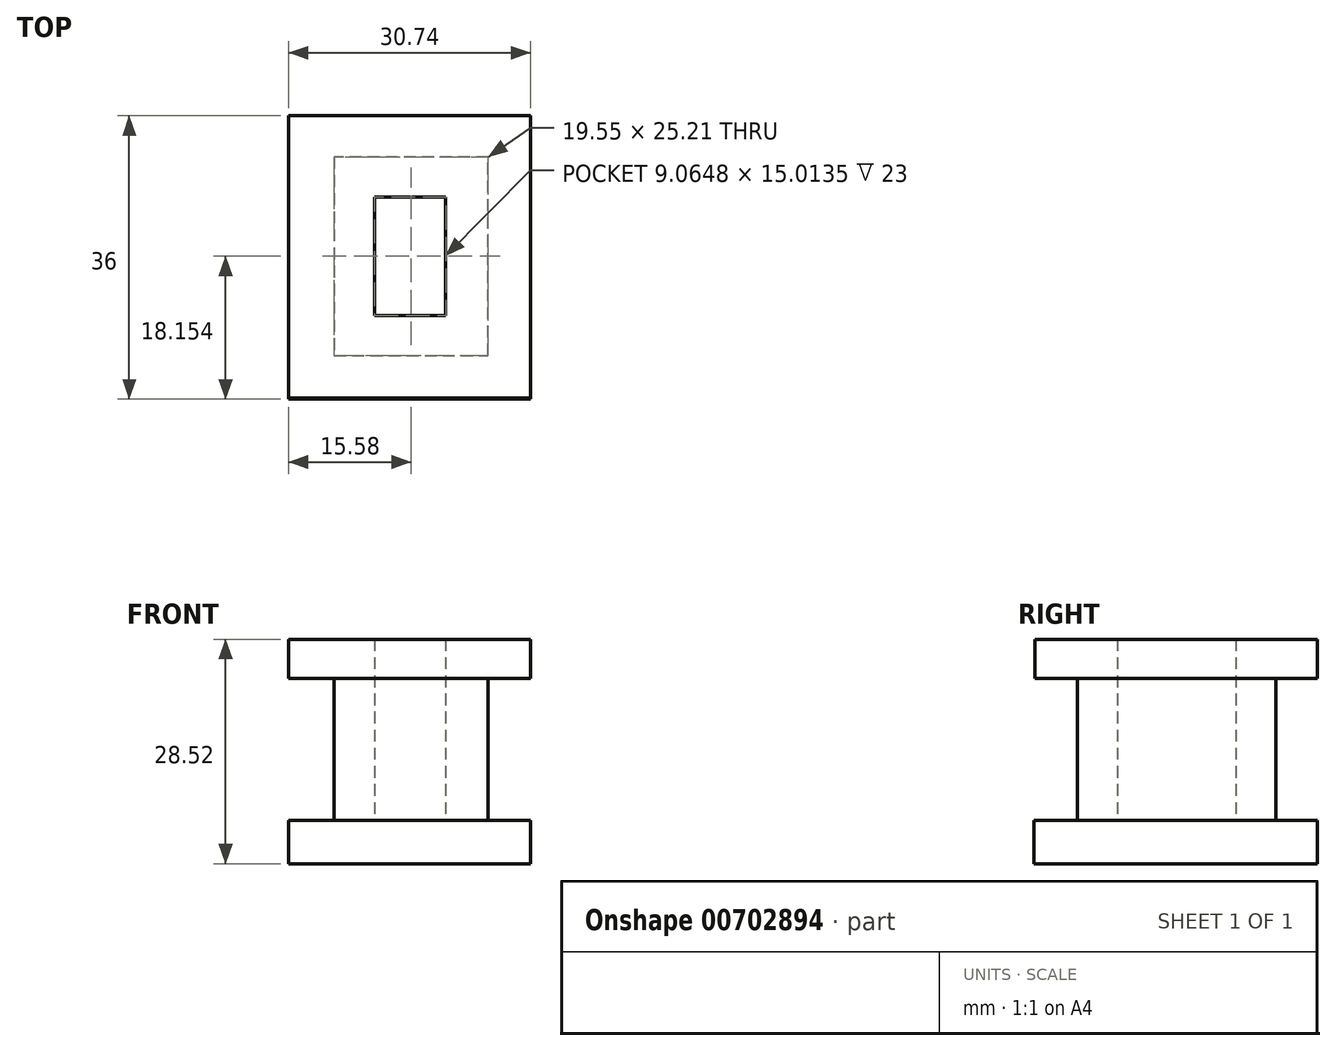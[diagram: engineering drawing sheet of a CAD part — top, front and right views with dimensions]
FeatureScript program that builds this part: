
annotation { "Feature Type Name" : "Feature", "Feature Type Description" : "" }
export const myFeature = defineFeature(function(context is Context, id is Id, definition is map)
    precondition{}
    {
        {
            var Q0;
            Q0=qCreatedBy(makeId("Front.planeOp"),FACE);
            var sketch = newSketch(context, id + "F0", { "sketchPlane" : qUnion([Q0])});
            skLineSegment(sketch, "E0", {"start": v(0, 0) * mm, "end": v(0, 5.52) * mm});
            skLineSegment(sketch, "E1", {"start": v(0, 5.52) * mm, "end": v(30.74, 5.52) * mm});
            skLineSegment(sketch, "E2", {"start": v(30.74, 5.52) * mm, "end": v(30.74, 0) * mm});
            skLineSegment(sketch, "E3", {"start": v(30.74, 0) * mm, "end": v(0, 0) * mm});
            skSolve(sketch);
        }
        {
            var Q0;
            Q0 = qSketchRegion(id + "F0", true);
            extrude(context, id + "F1", {"entities" : qUnion([Q0]), "depth" : 36 * mm, "offsetDistance" : 25 * mm});
        }
        {
            var Q0;
            Q0=makeQuery(id+"F1.opExtrude","SWEPT_FACE",FACE,{"disambiguationData":[OSD([sQuery(id+"F0.wireOp",EDGE,"E1")])]});
            var sketch = newSketch(context, id + "F2", { "sketchPlane" : qUnion([Q0])});
            skLineSegment(sketch, "E4", {"start": v(25.35, -18) * mm, "end": v(25.35, -5.24) * mm});
            skLineSegment(sketch, "E5", {"start": v(25.35, -5.24) * mm, "end": v(5.8, -5.24) * mm});
            skLineSegment(sketch, "E6", {"start": v(5.8, -5.24) * mm, "end": v(5.8, -30.45) * mm});
            skLineSegment(sketch, "E7", {"start": v(5.8, -30.45) * mm, "end": v(25.35, -30.45) * mm});
            skLineSegment(sketch, "E8", {"start": v(25.35, -30.45) * mm, "end": v(25.35, -18) * mm});
            skLineSegment(sketch, "E9", {"start": v(15.58, -25.35) * mm, "end": v(19.97, -25.35) * mm});
            skLineSegment(sketch, "E10", {"start": v(19.97, -25.35) * mm, "end": v(19.97, -10.34) * mm});
            skLineSegment(sketch, "E11", {"start": v(19.97, -10.34) * mm, "end": v(10.9, -10.34) * mm});
            skLineSegment(sketch, "E12", {"start": v(10.9, -10.34) * mm, "end": v(10.9, -25.35) * mm});
            skLineSegment(sketch, "E13", {"start": v(10.9, -25.35) * mm, "end": v(15.58, -25.35) * mm});
            skSolve(sketch);
        }
        {
            var Q0;
            Q0 = qSketchRegion(id + "F2", true);
            extrude(context, id + "F3", {"entities" : qUnion([Q0]), "operationType" : NewBodyOperationType.ADD, "depth" : 18 * mm, "offsetDistance" : 25 * mm});
        }
        {
            var Q0;
            Q0=makeQuery(id+"F3.opExtrude","CAP_FACE",FACE,{"disambiguationData":[OSD([sQuery(id+"F2.wireOp",EDGE,"E4"),sQuery(id+"F2.wireOp",EDGE,"E5"),sQuery(id+"F2.wireOp",EDGE,"E6"),sQuery(id+"F2.wireOp",EDGE,"E7"),sQuery(id+"F2.wireOp",EDGE,"E8"),sQuery(id+"F2.wireOp",EDGE,"E9"),sQuery(id+"F2.wireOp",EDGE,"E10"),sQuery(id+"F2.wireOp",EDGE,"E11"),sQuery(id+"F2.wireOp",EDGE,"E12"),sQuery(id+"F2.wireOp",EDGE,"E13")])],"isStart":false});
            var sketch = newSketch(context, id + "F4", { "sketchPlane" : qUnion([Q0])});
            skLineSegment(sketch, "E14", {"start": v(0, 0) * mm, "end": v(30.74, 0) * mm});
            skLineSegment(sketch, "E15", {"start": v(30.74, 0) * mm, "end": v(30.74, -35.83) * mm});
            skLineSegment(sketch, "E16", {"start": v(30.74, -35.83) * mm, "end": v(0, -35.83) * mm});
            skLineSegment(sketch, "E17", {"start": v(0, -35.83) * mm, "end": v(0, 0) * mm});
            skLineSegment(sketch, "E18", {"start": v(10.9, -10.34) * mm, "end": v(19.97, -10.34) * mm});
            skLineSegment(sketch, "E19", {"start": v(19.97, -10.34) * mm, "end": v(19.97, -25.35) * mm});
            skLineSegment(sketch, "E20", {"start": v(19.97, -25.35) * mm, "end": v(10.9, -25.35) * mm});
            skLineSegment(sketch, "E21", {"start": v(10.9, -25.35) * mm, "end": v(10.9, -10.34) * mm});
            skSolve(sketch);
        }
        {
            var Q0;
            Q0 = qSketchRegion(id + "F4", true);
            extrude(context, id + "F5", {"entities" : qUnion([Q0]), "operationType" : NewBodyOperationType.ADD, "depth" : 5 * mm, "offsetDistance" : 25 * mm});
        }
    });
